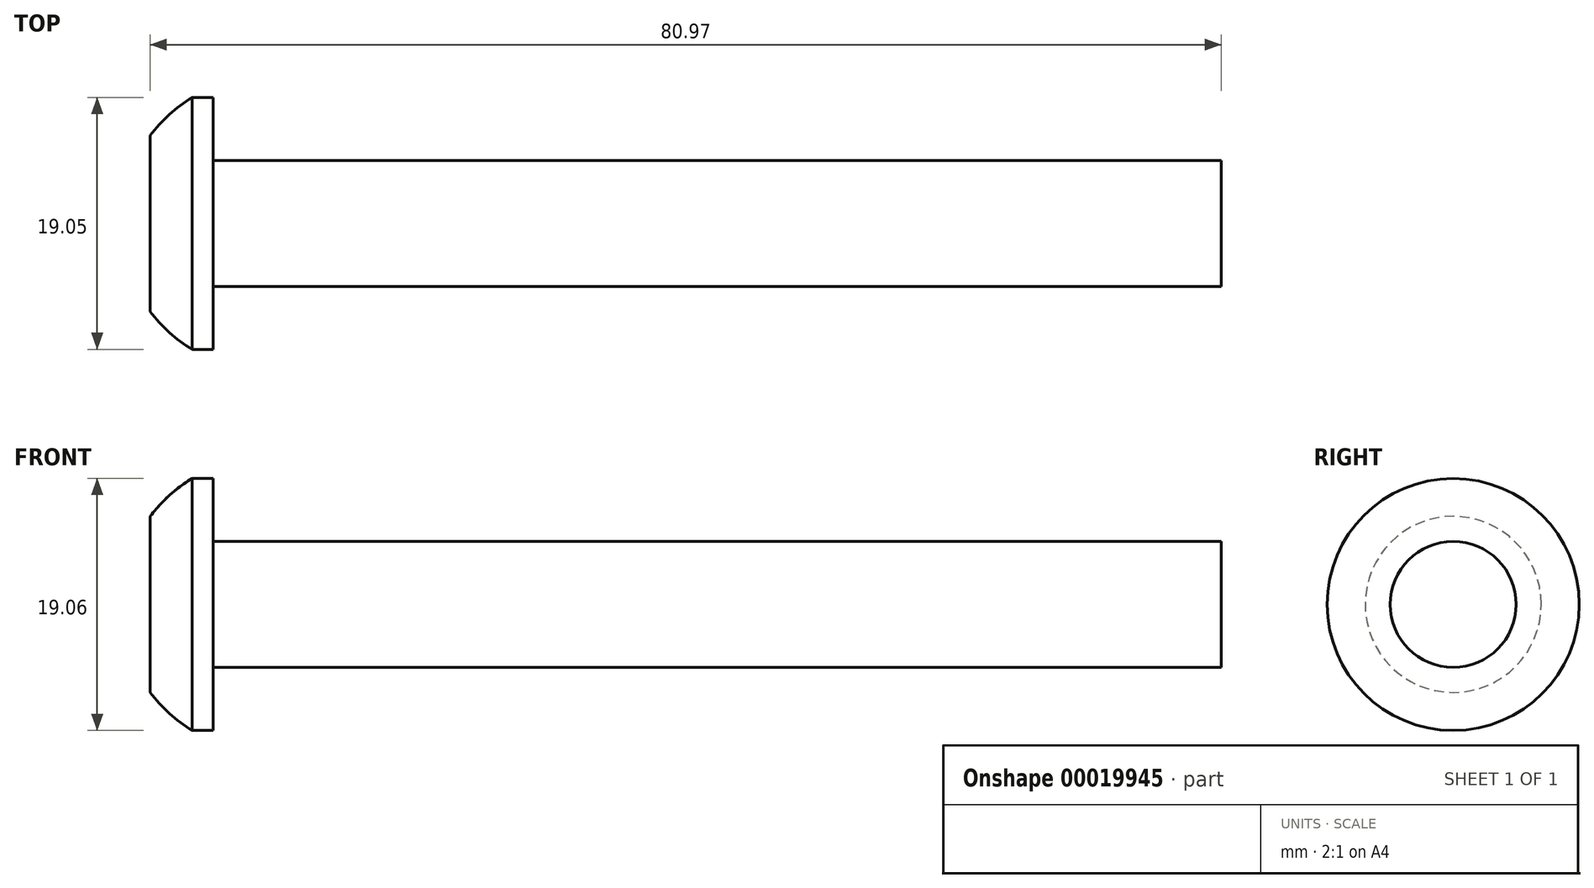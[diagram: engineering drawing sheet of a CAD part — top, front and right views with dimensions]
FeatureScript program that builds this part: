
annotation { "Feature Type Name" : "Feature", "Feature Type Description" : "" }
export const myFeature = defineFeature(function(context is Context, id is Id, definition is map)
    precondition{}
    {
        {
            var Q0;
            Q0=qCreatedBy(makeId("Top.planeOp"),FACE);
            var sketch = newSketch(context, id + "F0", { "sketchPlane" : qUnion([Q0])});
            skLineSegment(sketch, "E0", {"start": v(45.95, 23.36) * mm, "end": v(-30.25, 23.36) * mm});
            skLineSegment(sketch, "E1", {"start": v(-30.25, 23.36) * mm, "end": v(-30.25, 28.13) * mm});
            skLineSegment(sketch, "E2", {"start": v(-30.25, 28.13) * mm, "end": v(-31.84, 28.13) * mm});
            skLineSegment(sketch, "E3", {"start": v(-35.02, 18.6) * mm, "end": v(45.95, 18.6) * mm});
            skLineSegment(sketch, "E4", {"start": v(45.95, 18.6) * mm, "end": v(45.95, 23.36) * mm});
            skLineSegment(sketch, "E5", {"start": v(-35.02, 25.26) * mm, "end": v(-35.02, 18.6) * mm});
            skArc(sketch, "E6.trimOffspring", {"start": v(-31.84, 28.13) * mm, "mid": v(-33.57, 26.84) * mm, "end": v(-35.02, 25.26) * mm});
            skSolve(sketch);
        }
        {
            var Q0;
            Q0=makeQuery(id+"F0.imprint","IMPRINT",FACE,{"disambiguationData":[TD([[makeQuery(id+"F0.imprint","IMPRINT",EDGE,{"derivedFrom":sQuery(id+"F0.wireOp",EDGE,"E0")}),1.0]])]});
            var Q1;
            Q1=sQuery(id+"F0.wireOp",EDGE,"E3");
            revolve(context, id + "F1", {"entities" : qUnion([Q0]), "axis" : qUnion([Q1]), "revolveType" : RevolveType.FULL});
        }
    });
